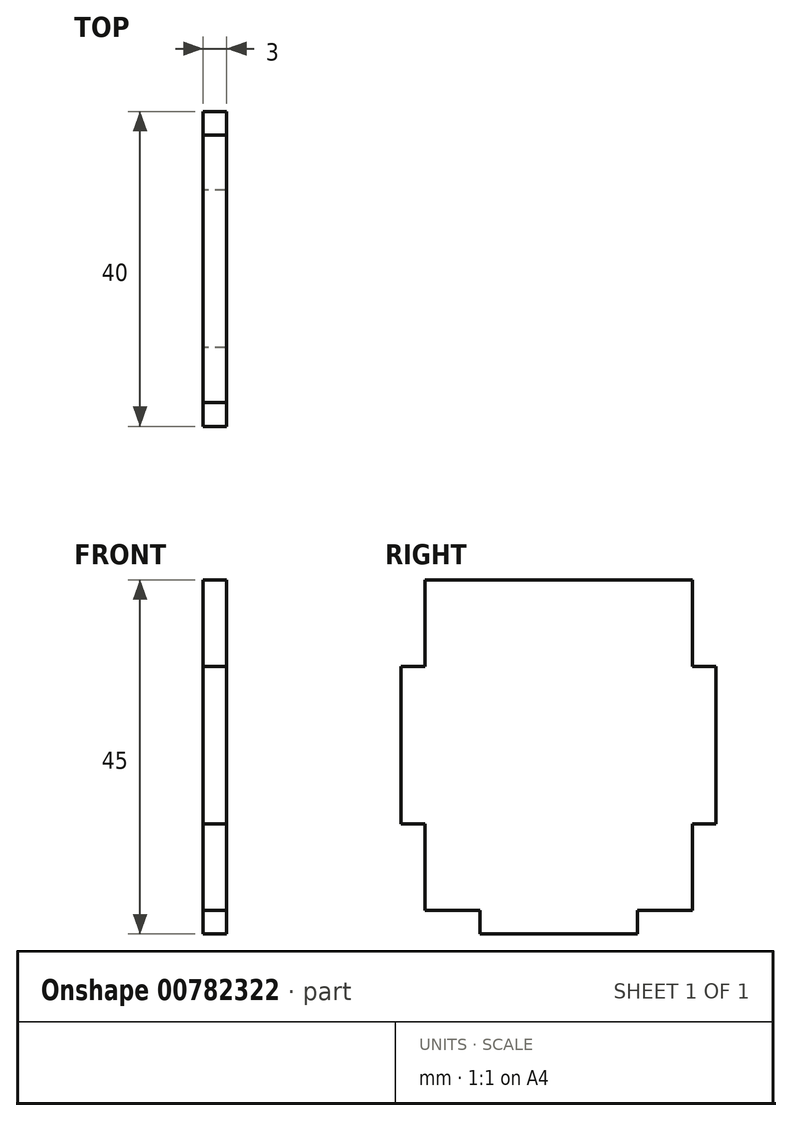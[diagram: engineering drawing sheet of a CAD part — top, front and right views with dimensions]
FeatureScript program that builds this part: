
annotation { "Feature Type Name" : "Feature", "Feature Type Description" : "" }
export const myFeature = defineFeature(function(context is Context, id is Id, definition is map)
    precondition{}
    {
        {
            var Q0;
            Q0=qCreatedBy(makeId("Right.planeOp"),FACE);
            var sketch = newSketch(context, id + "F0", { "sketchPlane" : qUnion([Q0])});
            skLineSegment(sketch, "E0.bottom", {"start": v(17, 21) * mm, "end": v(-17, 21) * mm});
            skLineSegment(sketch, "E0.top", {"start": v(17, -21) * mm, "end": v(-17, -21) * mm});
            skLineSegment(sketch, "E0.left", {"start": v(17, 21) * mm, "end": v(17, -21) * mm});
            skLineSegment(sketch, "E0.right", {"start": v(-17, 21) * mm, "end": v(-17, -21) * mm});
            skPoint(sketch, "E0.middle", {"position": v(0, 0) * mm});
            skLineSegment(sketch, "E1", {"start": v(-10, -21) * mm, "end": v(-10, -24) * mm});
            skLineSegment(sketch, "E2", {"start": v(-10, -24) * mm, "end": v(10, -24) * mm});
            skLineSegment(sketch, "E3", {"start": v(10, -24) * mm, "end": v(10, -21) * mm});
            skLineSegment(sketch, "E4", {"start": v(17, -10) * mm, "end": v(20, -10) * mm});
            skLineSegment(sketch, "E5", {"start": v(20, -10) * mm, "end": v(20, 10) * mm});
            skLineSegment(sketch, "E6", {"start": v(20, 10) * mm, "end": v(17, 10) * mm});
            skLineSegment(sketch, "E7.MirrorCS", {"start": v(-20, 10) * mm, "end": v(-17, 10) * mm});
            skLineSegment(sketch, "E8.MirrorCS", {"start": v(-20, -10) * mm, "end": v(-20, 10) * mm});
            skLineSegment(sketch, "E9.MirrorCS", {"start": v(-17, -10) * mm, "end": v(-20, -10) * mm});
            skSolve(sketch);
        }
        {
            var Q0;
            Q0 = qSketchRegion(id + "F0", true);
            extrude(context, id + "F1", {"entities" : qUnion([Q0]), "depth" : 3 * mm, "offsetDistance" : 25 * mm});
        }
    });
